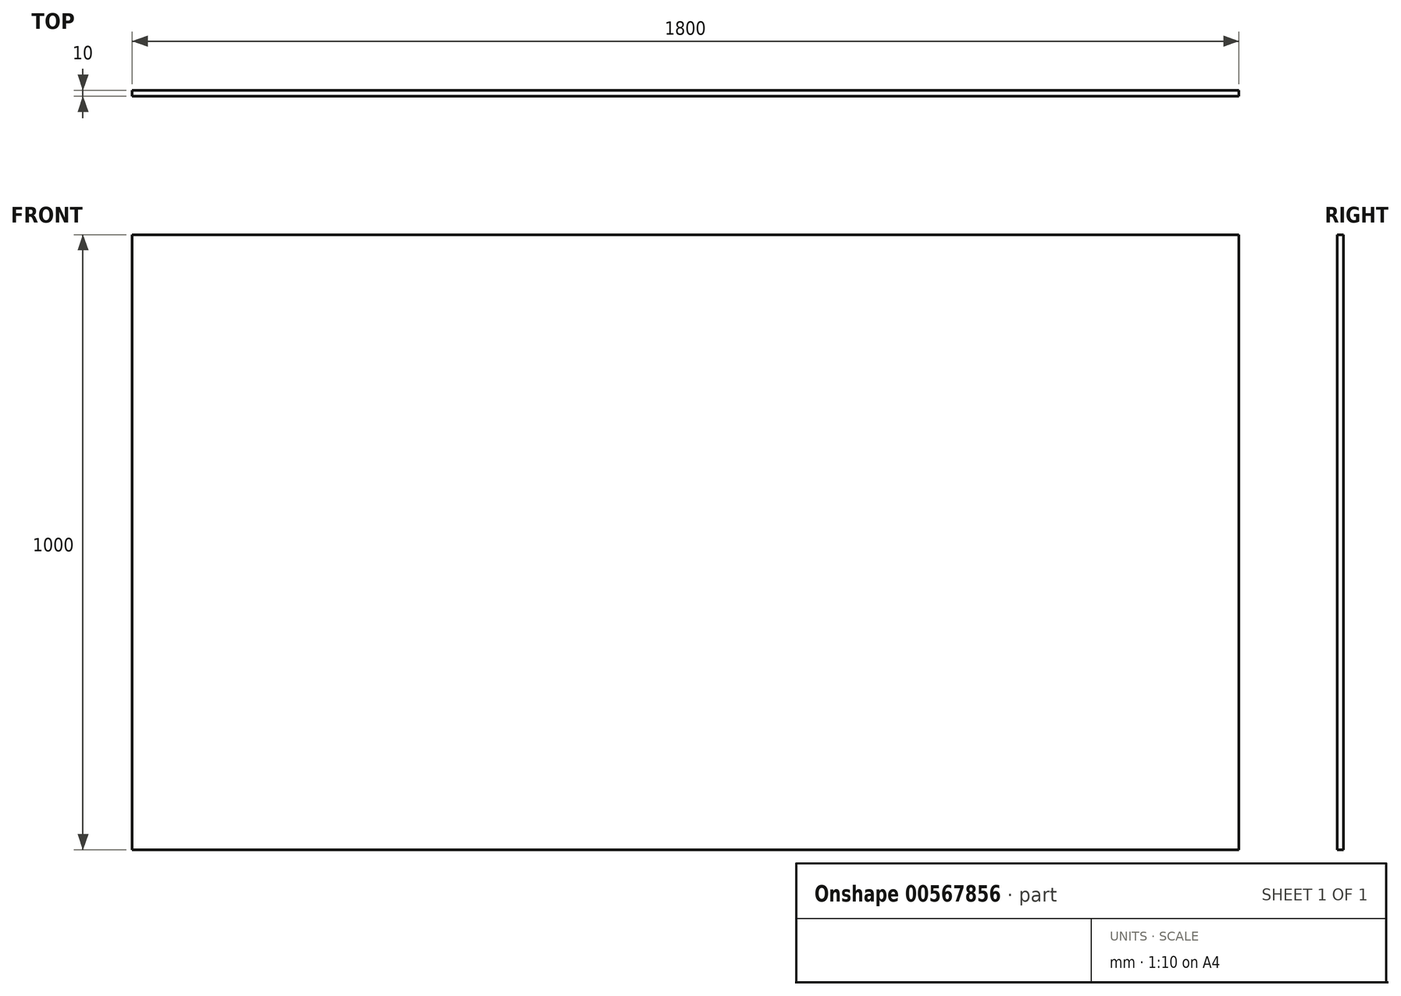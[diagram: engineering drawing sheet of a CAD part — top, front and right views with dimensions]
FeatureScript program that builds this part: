
annotation { "Feature Type Name" : "Feature", "Feature Type Description" : "" }
export const myFeature = defineFeature(function(context is Context, id is Id, definition is map)
    precondition{}
    {
        {
            var Q0;
            Q0=qCreatedBy(makeId("Front.planeOp"),FACE);
            var sketch = newSketch(context, id + "F0", { "sketchPlane" : qUnion([Q0])});
            skLineSegment(sketch, "E0.bottom", {"start": v(-393.28, 936.68) * mm, "end": v(1406.72, 936.68) * mm});
            skLineSegment(sketch, "E0.top", {"start": v(-393.28, -63.32) * mm, "end": v(1406.72, -63.32) * mm});
            skLineSegment(sketch, "E0.left", {"start": v(-393.28, 936.68) * mm, "end": v(-393.28, -63.32) * mm});
            skLineSegment(sketch, "E0.right", {"start": v(1406.72, 936.68) * mm, "end": v(1406.72, -63.32) * mm});
            skSolve(sketch);
        }
        {
            var Q0;
            Q0=makeQuery(id+"F0.imprint","IMPRINT",FACE,{"disambiguationData":[TD([[makeQuery(id+"F0.imprint","IMPRINT",EDGE,{"derivedFrom":sQuery(id+"F0.wireOp",EDGE,"E0.bottom")}),-1.0]])]});
            extrude(context, id + "F1", {"entities" : qUnion([Q0]), "depth" : 10 * mm, "offsetDistance" : 25 * mm});
        }
    });
